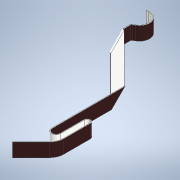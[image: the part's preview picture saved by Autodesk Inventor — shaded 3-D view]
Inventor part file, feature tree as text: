
AUTODESK INVENTOR PART (.ipt)
format: ipt  version: 2021 (Build 250183000, 183)  size: 223,744 bytes
history: native  units: mm
features: sketch x8, other x7, extrude x1
ambient origin geometry x8: Origin, YZ Plane, XZ Plane, XY Plane, X Axis, Y Axis, Z Axis, Center Point
bodies: Solid1 (feature_tree)
feature tree (16):
  extrude  "Extrusion1"  Depth=10.0mm
  other  "Bend Part1"
  other  "Bend Part19"
  other  "Bend Part20"
  other  "Bend Part21"
  other  "Bend Part22"
  other  "Bend Part23"
  other  "Bend Part24"
  sketch  "Sketch1"  dims[d0=200.0mm d1=10.0mm]
  sketch  "Sketch2"  dims[d2=0.5mm d3=0.0mm]
  sketch  "Sketch23"  dims[d4=2.0mm]
  sketch  "Sketch24"  dims[d5=7.0mm d6=150.0deg]
  sketch  "Sketch25"  dims[d69=1.0mm d70=60.0deg]
  sketch  "Sketch27"  dims[d71=2.0mm]
  sketch  "Sketch28"  dims[d72=45.0deg]
  sketch  "Sketch30"  dims[d73=5.0mm d74=0.1mm d75=180.0deg d76=45.0deg d77=26.0mm d78=0.1mm d79=180.0deg d80=3.0mm d81=180.0deg d82=2.0mm d83=180.0deg d84=10.0mm d85=45.0deg d86=20.0mm]
